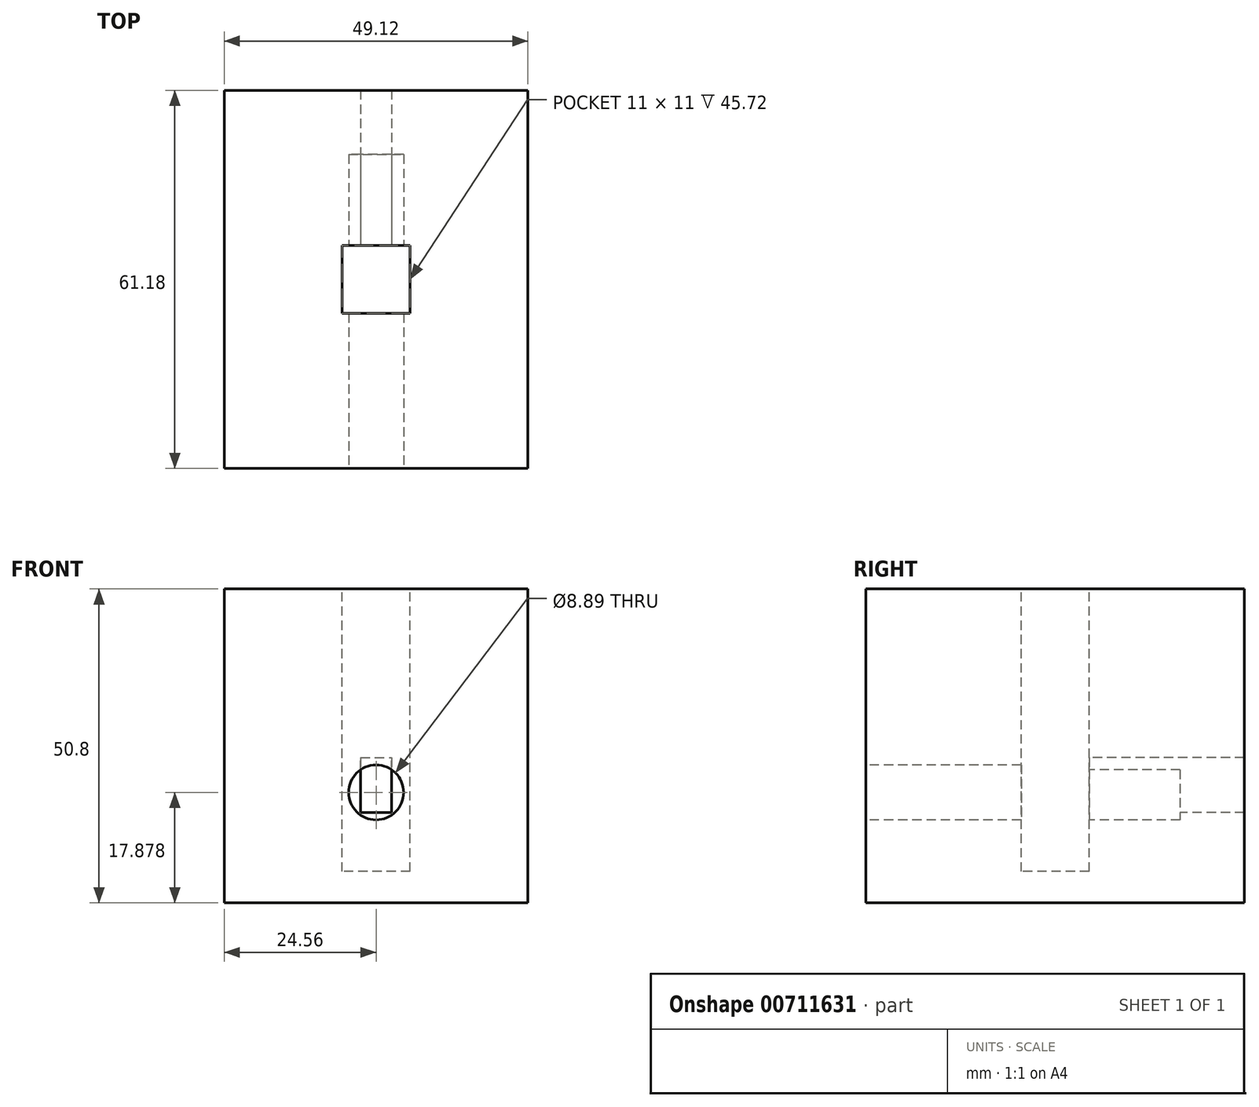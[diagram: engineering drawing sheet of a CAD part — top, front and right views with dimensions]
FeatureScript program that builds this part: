
annotation { "Feature Type Name" : "Feature", "Feature Type Description" : "" }
export const myFeature = defineFeature(function(context is Context, id is Id, definition is map)
    precondition{}
    {
        {
            var Q0;
            Q0=qCreatedBy(makeId("Top.planeOp"),FACE);
            var sketch = newSketch(context, id + "F0", { "sketchPlane" : qUnion([Q0])});
            skLineSegment(sketch, "E0.bottom", {"start": v(24.56, 30.6) * mm, "end": v(-24.56, 30.6) * mm});
            skLineSegment(sketch, "E0.top", {"start": v(24.56, -30.6) * mm, "end": v(-24.56, -30.6) * mm});
            skLineSegment(sketch, "E0.left", {"start": v(24.56, 30.6) * mm, "end": v(24.56, -30.6) * mm});
            skLineSegment(sketch, "E0.right", {"start": v(-24.56, 30.6) * mm, "end": v(-24.56, -30.6) * mm});
            skPoint(sketch, "E0.middle", {"position": v(0, 0) * mm});
            skSolve(sketch);
        }
        {
            var Q0;
            Q0 = qSketchRegion(id + "F0", true);
            extrude(context, id + "F1", {"entities" : qUnion([Q0]), "depth" : 50.8 * mm, "offsetDistance" : 25.4 * mm});
        }
        {
            var Q0;
            Q0=makeQuery(id+"F1.opExtrude","CAP_FACE",FACE,{"disambiguationData":[OSD([sQuery(id+"F0.wireOp",EDGE,"E0.bottom"),sQuery(id+"F0.wireOp",EDGE,"E0.top"),sQuery(id+"F0.wireOp",EDGE,"E0.left"),sQuery(id+"F0.wireOp",EDGE,"E0.right")])],"isStart":false});
            var sketch = newSketch(context, id + "F2", { "sketchPlane" : qUnion([Q0])});
            skLineSegment(sketch, "E1.bottom", {"start": v(5.5, 5.5) * mm, "end": v(-5.5, 5.5) * mm});
            skLineSegment(sketch, "E1.top", {"start": v(5.5, -5.5) * mm, "end": v(-5.5, -5.5) * mm});
            skLineSegment(sketch, "E1.left", {"start": v(5.5, 5.5) * mm, "end": v(5.5, -5.5) * mm});
            skLineSegment(sketch, "E1.right", {"start": v(-5.5, 5.5) * mm, "end": v(-5.5, -5.5) * mm});
            skPoint(sketch, "E1.middle", {"position": v(0, 0) * mm});
            skSolve(sketch);
        }
        {
            var Q0;
            Q0=makeQuery(id+"F2.imprint","IMPRINT",FACE,{"disambiguationData":[TD([[makeQuery(id+"F2.imprint","IMPRINT",EDGE,{"derivedFrom":sQuery(id+"F2.wireOp",EDGE,"E1.bottom")}),1.0]])]});
            extrude(context, id + "F3", {"entities" : qUnion([Q0]), "operationType" : NewBodyOperationType.REMOVE, "oppositeDirection" : true, "depth" : 45.72 * mm, "offsetDistance" : 25.4 * mm});
        }
        {
            var Q0;
            Q0=qCreatedBy(makeId("Front.planeOp"),FACE);
            var sketch = newSketch(context, id + "F4", { "sketchPlane" : qUnion([Q0])});
            skLineSegment(sketch, "E2", {"start": v(0, 0) * mm, "end": v(0, 19.05) * mm});
            skLineSegment(sketch, "E3.bottom", {"start": v(-2.5, 14.6) * mm, "end": v(2.5, 14.6) * mm});
            skLineSegment(sketch, "E3.top", {"start": v(-2.5, 23.5) * mm, "end": v(2.5, 23.5) * mm});
            skLineSegment(sketch, "E3.left", {"start": v(-2.5, 14.6) * mm, "end": v(-2.5, 23.5) * mm});
            skLineSegment(sketch, "E3.right", {"start": v(2.5, 14.6) * mm, "end": v(2.5, 23.5) * mm});
            skPoint(sketch, "E3.middle", {"position": v(0, 19.05) * mm});
            skLineSegment(sketch, "E4.left", {"start": v(-39.02, 87.76) * mm, "end": v(-39.02, 88.25) * mm});
            skLineSegment(sketch, "E4.right", {"start": v(-10.6, 87.76) * mm, "end": v(-10.6, 88.25) * mm});
            skPoint(sketch, "E4.middle", {"position": v(-24.8, 88) * mm});
            skSolve(sketch);
        }
        {
            var Q0;
            Q0=makeQuery(id+"F1.opExtrude","SWEPT_FACE",FACE,{"disambiguationData":[OSD([sQuery(id+"F0.wireOp",EDGE,"E0.top")])]});
            var sketch = newSketch(context, id + "F5", { "sketchPlane" : qUnion([Q0])});
            skLineSegment(sketch, "E5", {"start": v(0, 0) * mm, "end": v(0, 17.88) * mm});
            skCircle(sketch, "E6", {"center": v(0, 17.88) * mm, "radius": 4.45 * mm});
            skSolve(sketch);
        }
        {
            var Q0;
            Q0 = qSketchRegion(id + "F4", true);
            extrude(context, id + "F6", {"entities" : qUnion([Q0]), "operationType" : NewBodyOperationType.REMOVE, "oppositeDirection" : true, "depth" : 50.8 * mm, "offsetDistance" : 25.4 * mm});
        }
        {
            var Q0;
            Q0=makeQuery(id+"F5.imprint","IMPRINT",FACE,{"disambiguationData":[TD([[makeQuery(id+"F5.imprint","IMPRINT",EDGE,{"derivedFrom":sQuery(id+"F5.wireOp",EDGE,"E6")}),1.0]])]});
            extrude(context, id + "F7", {"entities" : qUnion([Q0]), "operationType" : NewBodyOperationType.REMOVE, "oppositeDirection" : true, "depth" : 50.8 * mm, "offsetDistance" : 25.4 * mm});
        }
    });
